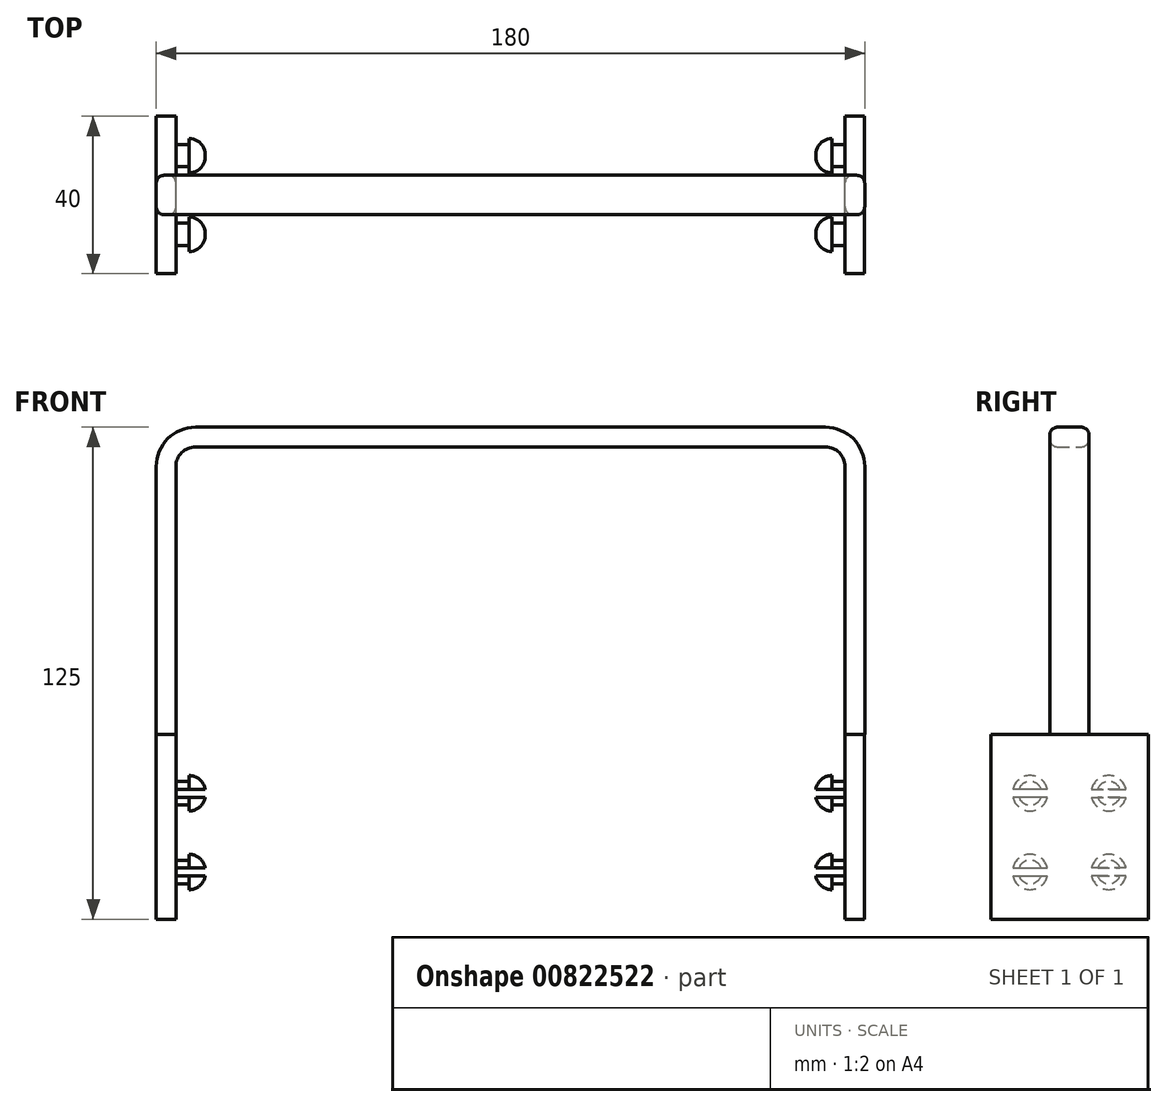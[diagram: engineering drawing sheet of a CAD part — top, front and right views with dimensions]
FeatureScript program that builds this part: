
annotation { "Feature Type Name" : "Feature", "Feature Type Description" : "" }
export const myFeature = defineFeature(function(context is Context, id is Id, definition is map)
    precondition{}
    {
        {
            var Q0;
            Q0=qCreatedBy(makeId("Front.planeOp"),FACE);
            var sketch = newSketch(context, id + "F0", { "sketchPlane" : qUnion([Q0])});
            skLineSegment(sketch, "E0", {"start": v(0, 78) * mm, "end": v(-80, 78) * mm});
            skLineSegment(sketch, "E1", {"start": v(-90, 68) * mm, "end": v(-90, 0) * mm});
            skLineSegment(sketch, "E2", {"start": v(-90, 0) * mm, "end": v(-85, 0) * mm});
            skLineSegment(sketch, "E3", {"start": v(-85, 0) * mm, "end": v(-85, 68) * mm});
            skLineSegment(sketch, "E4", {"start": v(-80, 73) * mm, "end": v(0, 73) * mm});
            skLineSegment(sketch, "E5", {"start": v(0, 98.55) * mm, "end": v(0, -22.25) * mm, "construction": true});
            skPoint(sketch, "E6.visualSharp", {"position": v(-85, 73) * mm});
            skArc(sketch, "E6.filletArc", {"start": v(-80, 73) * mm, "mid": v(-83.54, 71.54) * mm, "end": v(-85, 68) * mm});
            skPoint(sketch, "E7.visualSharp", {"position": v(-90, 78) * mm});
            skArc(sketch, "E7.filletArc", {"start": v(-80, 78) * mm, "mid": v(-87.07, 75.07) * mm, "end": v(-90, 68) * mm});
            skLineSegment(sketch, "E8.MirrorCS", {"start": v(90, 0) * mm, "end": v(85, 0) * mm});
            skArc(sketch, "E9.MirrorCS", {"start": v(80, 78) * mm, "mid": v(87.07, 75.07) * mm, "end": v(90, 68) * mm});
            skLineSegment(sketch, "E10.MirrorCS", {"start": v(0, 78) * mm, "end": v(80, 78) * mm});
            skPoint(sketch, "E11.MirrorP", {"position": v(90, 78) * mm});
            skLineSegment(sketch, "E12.MirrorCS", {"start": v(90, 68) * mm, "end": v(90, 0) * mm});
            skLineSegment(sketch, "E13.MirrorCS", {"start": v(85, 0) * mm, "end": v(85, 68) * mm});
            skPoint(sketch, "E14.MirrorP", {"position": v(85, 73) * mm});
            skArc(sketch, "E15.MirrorCS", {"start": v(80, 73) * mm, "mid": v(83.54, 71.54) * mm, "end": v(85, 68) * mm});
            skLineSegment(sketch, "E16.MirrorCS", {"start": v(80, 73) * mm, "end": v(0, 73) * mm});
            skSolve(sketch);
        }
        {
            var Q0;
            Q0=qSketchRegion(id+"F0",true);
            extrude(context, id + "F1", {"entities" : qUnion([Q0]), "depth" : 10 * mm, "offsetDistance" : 25 * mm});
        }
        {
            var Q0;
            Q0=makeQuery(id+"F1.opExtrude","CAP_EDGE",EDGE,{"disambiguationData":[OSD([sQuery(id+"F0.wireOp",EDGE,"E0"),sQuery(id+"F0.wireOp",EDGE,"E10.MirrorCS")])],"isStart":false});
            var Q1;
            Q1=makeQuery(id+"F1.opExtrude","CAP_EDGE",EDGE,{"disambiguationData":[OSD([sQuery(id+"F0.wireOp",EDGE,"E4"),sQuery(id+"F0.wireOp",EDGE,"E16.MirrorCS")])],"isStart":false});
            var Q2;
            Q2=makeQuery(id+"F1.opExtrude","CAP_EDGE",EDGE,{"disambiguationData":[OSD([sQuery(id+"F0.wireOp",EDGE,"E12.MirrorCS")])],"isStart":true});
            var Q3;
            Q3=makeQuery(id+"F1.opExtrude","CAP_EDGE",EDGE,{"disambiguationData":[OSD([sQuery(id+"F0.wireOp",EDGE,"E13.MirrorCS")])],"isStart":true});
            fillet(context, id + "F2", {"entities" : qUnion([Q0, Q1, Q2, Q3]), "radius" : 2 * mm, "tangentPropagation" : true, "allowEdgeOverflow" : false});
        }
        {
            var Q0;
            Q0=makeQuery(id+"F1.opExtrude","SWEPT_FACE",FACE,{"disambiguationData":[OSD([sQuery(id+"F0.wireOp",EDGE,"E2")])]});
            var sketch = newSketch(context, id + "F3", { "sketchPlane" : qUnion([Q0])});
            skPoint(sketch, "E17.oppositeSnap0", {"position": v(-84.98, 5) * mm});
            skLineSegment(sketch, "E17.bottom", {"start": v(-89.98, 25) * mm, "end": v(-84.98, 25) * mm});
            skLineSegment(sketch, "E17.top", {"start": v(-89.98, -15) * mm, "end": v(-84.98, -15) * mm});
            skLineSegment(sketch, "E17.left", {"start": v(-89.98, 25) * mm, "end": v(-89.98, -15) * mm});
            skLineSegment(sketch, "E17.right", {"start": v(-84.98, 25) * mm, "end": v(-84.98, -15) * mm});
            skLineSegment(sketch, "E18", {"start": v(0, 36.49) * mm, "end": v(0, -20.35) * mm, "construction": true});
            skLineSegment(sketch, "E19.MirrorCS", {"start": v(89.98, 25) * mm, "end": v(84.98, 25) * mm});
            skLineSegment(sketch, "E20.MirrorCS", {"start": v(89.98, -15) * mm, "end": v(84.98, -15) * mm});
            skPoint(sketch, "E21.MirrorP", {"position": v(84.98, 5) * mm});
            skLineSegment(sketch, "E22.MirrorCS", {"start": v(89.98, 25) * mm, "end": v(89.98, -15) * mm});
            skLineSegment(sketch, "E23.MirrorCS", {"start": v(84.98, 25) * mm, "end": v(84.98, -15) * mm});
            skSolve(sketch);
        }
        {
            var Q0;
            Q0=qSketchRegion(id+"F3",true);
            extrude(context, id + "F4", {"entities" : qUnion([Q0]), "operationType" : NewBodyOperationType.ADD, "depth" : 47 * mm, "offsetDistance" : 25 * mm});
        }
        {
            var Q0;
            Q0=makeQuery(id+"F4.opExtrude","SWEPT_FACE",FACE,{"disambiguationData":[OSD([sQuery(id+"F3.wireOp",EDGE,"E17.left")])]});
            var sketch = newSketch(context, id + "F5", { "sketchPlane" : qUnion([Q0])});
            skLineSegment(sketch, "E24", {"start": v(5, 10.28) * mm, "end": v(5, -104.28) * mm, "construction": true});
            skCircle(sketch, "E25", {"center": v(15, -15) * mm, "radius": 3 * mm});
            skCircle(sketch, "E26", {"center": v(-5, -35) * mm, "radius": 3 * mm});
            skSolve(sketch);
        }
        {
            var Q0;
            Q0=qSketchRegion(id+"F5",true);
            extrude(context, id + "F6", {"entities" : qUnion([Q0]), "operationType" : NewBodyOperationType.ADD, "oppositeDirection" : true, "depth" : 8.3 * mm, "offsetDistance" : 25 * mm});
        }
        {
            var Q0;
            Q0=makeQuery(id+"F4.opExtrude","SWEPT_FACE",FACE,{"disambiguationData":[OSD([sQuery(id+"F3.wireOp",EDGE,"E22.MirrorCS")])]});
            var sketch = newSketch(context, id + "F7", { "sketchPlane" : qUnion([Q0])});
            skLineSegment(sketch, "E27", {"start": v(-5, 8.5) * mm, "end": v(-5, -102.5) * mm, "construction": true});
            skPoint(sketch, "E28", {"position": v(-5, 0) * mm});
            skCircle(sketch, "E29", {"center": v(5, -15) * mm, "radius": 3 * mm});
            skCircle(sketch, "E30", {"center": v(-15, -35) * mm, "radius": 3 * mm});
            skSolve(sketch);
        }
        {
            var Q0;
            Q0=qSketchRegion(id+"F7",true);
            extrude(context, id + "F8", {"entities" : qUnion([Q0]), "operationType" : NewBodyOperationType.ADD, "oppositeDirection" : true, "depth" : 8.3 * mm, "offsetDistance" : 25 * mm});
        }
        {
            var Q0;
            Q0=makeQuery(id+"F8.opExtrude","CAP_FACE",FACE,{"disambiguationData":[OSD([sQuery(id+"F7.wireOp",EDGE,"E29")])],"isStart":false});
            var sketch = newSketch(context, id + "F9", { "sketchPlane" : qUnion([Q0])});
            skCircle(sketch, "E31", {"center": v(-5, -15) * mm, "radius": 4.5 * mm});
            skCircle(sketch, "E32", {"center": v(15, -35) * mm, "radius": 4.5 * mm});
            skSolve(sketch);
        }
        {
            var Q0;
            Q0=qSketchRegion(id+"F9",true);
            extrude(context, id + "F10", {"entities" : qUnion([Q0]), "operationType" : NewBodyOperationType.ADD, "depth" : 4.2 * mm, "offsetDistance" : 25 * mm});
        }
        {
            var Q0;
            Q0=makeQuery(id+"F10.opExtrude","CAP_EDGE",EDGE,{"disambiguationData":[OSD([sQuery(id+"F9.wireOp",EDGE,"E31")])],"isStart":false});
            var Q1;
            Q1=makeQuery(id+"F10.opExtrude","CAP_EDGE",EDGE,{"disambiguationData":[OSD([sQuery(id+"F9.wireOp",EDGE,"E32")])],"isStart":false});
            fillet(context, id + "F11", {"entities" : qUnion([Q0, Q1]), "radius" : 4.2 * mm, "tangentPropagation" : true, "allowEdgeOverflow" : false});
        }
        {
            var Q0;
            Q0=makeQuery(id+"F6.opExtrude","CAP_FACE",FACE,{"disambiguationData":[OSD([sQuery(id+"F5.wireOp",EDGE,"E25")])],"isStart":false});
            var sketch = newSketch(context, id + "F12", { "sketchPlane" : qUnion([Q0])});
            skCircle(sketch, "E33", {"center": v(-15, -15) * mm, "radius": 4.5 * mm});
            skCircle(sketch, "E34", {"center": v(5, -35) * mm, "radius": 4.5 * mm});
            skSolve(sketch);
        }
        {
            var Q0;
            Q0=qSketchRegion(id+"F12",true);
            extrude(context, id + "F13", {"entities" : qUnion([Q0]), "operationType" : NewBodyOperationType.ADD, "depth" : 4.2 * mm, "offsetDistance" : 25 * mm});
        }
        {
            var Q0;
            Q0=makeQuery(id+"F13.opExtrude","CAP_EDGE",EDGE,{"disambiguationData":[OSD([sQuery(id+"F12.wireOp",EDGE,"E33")])],"isStart":false});
            var Q1;
            Q1=makeQuery(id+"F13.opExtrude","CAP_EDGE",EDGE,{"disambiguationData":[OSD([sQuery(id+"F12.wireOp",EDGE,"E34")])],"isStart":false});
            fillet(context, id + "F14", {"entities" : qUnion([Q0, Q1]), "radius" : 4.2 * mm, "tangentPropagation" : true, "allowEdgeOverflow" : false});
        }
        {
            var Q0;
            Q0=qCreatedBy(makeId("Top.planeOp"),FACE);
            cPlane(context, id + "F15", {"entities" : qUnion([Q0]), "cplaneType" : CPlaneType.OFFSET, "offset" : 16 * mm, "oppositeDirection" : true, "width" : 150 * mm, "height" : 150 * mm});
        }
        {
            var Q0;
            Q0=qCreatedBy(id+"F15.planeOp",FACE);
            var sketch = newSketch(context, id + "F16", { "sketchPlane" : qUnion([Q0])});
            skLineSegment(sketch, "E35.bottom", {"start": v(84.98, 11.73) * mm, "end": v(-84.98, 11.73) * mm});
            skLineSegment(sketch, "E35.top", {"start": v(84.98, -23.17) * mm, "end": v(-84.98, -23.17) * mm});
            skLineSegment(sketch, "E35.left", {"start": v(84.98, 11.73) * mm, "end": v(84.98, -23.17) * mm});
            skLineSegment(sketch, "E35.right", {"start": v(-84.98, 11.73) * mm, "end": v(-84.98, -23.17) * mm});
            skSolve(sketch);
        }
        {
            var Q0;
            Q0=qSketchRegion(id+"F16",true);
            extrude(context, id + "F17", {"entities" : qUnion([Q0]), "operationType" : NewBodyOperationType.REMOVE, "depth" : 2 * mm, "offsetDistance" : 25 * mm});
        }
        {
            var Q0;
            Q0=qCreatedBy(makeId("Top.planeOp"),FACE);
            cPlane(context, id + "F18", {"entities" : qUnion([Q0]), "cplaneType" : CPlaneType.OFFSET, "offset" : 36 * mm, "oppositeDirection" : true, "width" : 150 * mm, "height" : 150 * mm});
        }
        {
            var Q0;
            Q0=qCreatedBy(id+"F18.planeOp",FACE);
            var sketch = newSketch(context, id + "F19", { "sketchPlane" : qUnion([Q0])});
            skLineSegment(sketch, "E36.bottom", {"start": v(-84.98, -22.32) * mm, "end": v(84.98, -22.32) * mm});
            skLineSegment(sketch, "E36.top", {"start": v(-84.98, 12.23) * mm, "end": v(84.98, 12.23) * mm});
            skLineSegment(sketch, "E36.left", {"start": v(-84.98, -22.32) * mm, "end": v(-84.98, 12.23) * mm});
            skLineSegment(sketch, "E36.right", {"start": v(84.98, -22.32) * mm, "end": v(84.98, 12.23) * mm});
            skSolve(sketch);
        }
        {
            var Q0;
            Q0=qSketchRegion(id+"F19",true);
            extrude(context, id + "F20", {"entities" : qUnion([Q0]), "operationType" : NewBodyOperationType.REMOVE, "depth" : 2 * mm, "offsetDistance" : 25 * mm});
        }
    });
